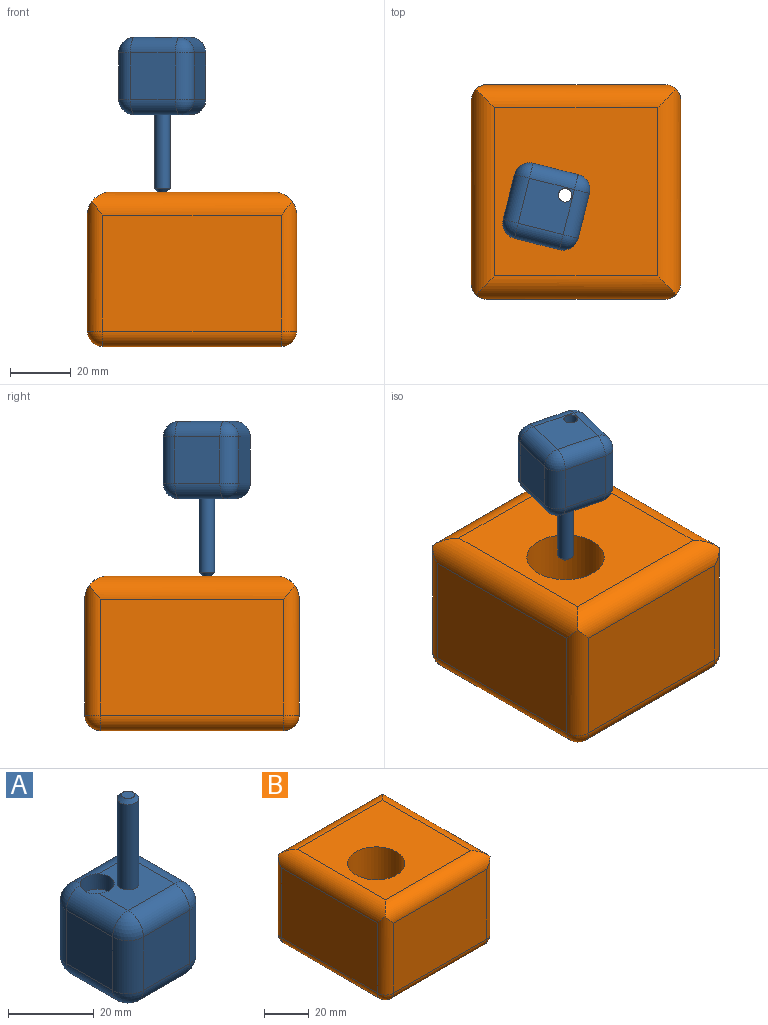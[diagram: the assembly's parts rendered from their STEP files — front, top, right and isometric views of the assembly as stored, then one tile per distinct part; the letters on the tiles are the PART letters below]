
ASSEMBLY  parts=2 mates=1
PART A: 32 faces, bbox 25.4x25.4x50.8 mm
  f0: plane 15.24x15.24mm, normal (0,0,1), area 174.5mm2, adj f2,f3,f19,f20,f28,f29
  f1: sphere r=5.08mm, area 40.3mm2, adj f2,f3,f9,f28
  f2: cylinder r=5.08mm len=15.24mm, axis (0,1,0), area 115.6mm2, adj f0,f1,f7,f15,f28
  f3: cylinder r=5.08mm len=15.24mm, axis (1,0,0), area 115.6mm2, adj f0,f1,f6,f16,f28
  f4: plane 15.24x15.24mm, normal (0,-1,0), area 232.3mm2, adj f14,f19,f22,f25
  f5: plane 15.24x15.24mm, normal (1,0,0), area 232.3mm2, adj f11,f20,f21,f25
  f6: plane 15.24x15.24mm, normal (0,1,0), area 232.3mm2, adj f3,f9,f11,f12
  f7: plane 15.24x15.24mm, normal (-1,0,0), area 232.3mm2, adj f2,f9,f13,f14
  f8: plane 15.24x15.24mm, normal (0,0,-1), area 216.4mm2, adj f12,f13,f21,f22,f26
  f9: cylinder r=5.08mm len=15.24mm, axis (0,0,1), area 121.6mm2, adj f1,f6,f7,f10
  f10: sphere r=5.08mm, area 40.5mm2, adj f9,f12,f13
  f11: cylinder r=5.08mm len=15.24mm, axis (0,0,-1), area 121.6mm2, adj f5,f6,f16,f17
  f12: cylinder r=5.08mm len=15.24mm, axis (-1,0,0), area 121.6mm2, adj f6,f8,f10,f17
  f13: cylinder r=5.08mm len=15.24mm, axis (0,-1,0), area 121.6mm2, adj f7,f8,f10,f18
  f14: cylinder r=5.08mm len=15.24mm, axis (0,0,-1), area 121.6mm2, adj f4,f7,f15,f18
  f15: sphere r=5.08mm, area 40.5mm2, adj f2,f14,f19
  f16: sphere r=5.08mm, area 40.5mm2, adj f3,f11,f20
  f17: sphere r=5.08mm, area 40.5mm2, adj f11,f12,f21
  f18: sphere r=5.08mm, area 40.5mm2, adj f13,f14,f22
  f19: cylinder r=5.08mm len=15.24mm, axis (-1,0,0), area 121.6mm2, adj f0,f4,f15,f23
  f20: cylinder r=5.08mm len=15.24mm, axis (0,-1,0), area 121.6mm2, adj f0,f5,f16,f23
  f21: cylinder r=5.08mm len=15.24mm, axis (0,1,0), area 121.6mm2, adj f5,f8,f17,f24
  f22: cylinder r=5.08mm len=15.24mm, axis (1,0,0), area 121.6mm2, adj f4,f8,f18,f24
  f23: sphere r=5.08mm, area 40.5mm2, adj f19,f20,f25
  f24: sphere r=5.08mm, area 40.5mm2, adj f21,f22,f25
  f25: cylinder r=5.08mm len=15.24mm, axis (0,0,1), area 121.6mm2, adj f4,f5,f23,f24
  f26: cylinder r=2.25mm len=21.03mm, axis (0,0,1), area 297mm2, adj f8,f27
  f27: plane 7.94x7.94mm, normal (0,0,1), area 33.6mm2, adj f26,f28
  f28: cylinder r=3.97mm len=7.94mm, axis (0,0,1), area 107.5mm2, adj f0,f1,f2,f3,f27
  f29: cylinder r=2.54mm len=24.4mm, axis (0,0,-1), area 389.4mm2, adj f0,f31
  f30: plane 3.08x3.08mm, normal (0,0,1), area 7.5mm2, adj f31
  f31: cone r=1.54mm half-angle=45deg, axis (0,0,-1), area 18.1mm2, adj f29,f30
PART B: 23 faces, bbox 68.8x70.5x50.8 mm
  f0: plane 58.65x38.1mm, normal (0,1,0), area 2234.6mm2, adj f6,f12,f18,f21
  f1: plane 60.33x38.1mm, normal (-1,0,0), area 2298.5mm2, adj f7,f10,f12,f13
  f2: plane 58.65x38.1mm, normal (0,-1,0), area 2234.6mm2, adj f9,f10,f14,f15
  f3: plane 60.33x38.1mm, normal (1,0,0), area 2298.5mm2, adj f8,f15,f19,f21
  f4: plane 55.25x53.57mm, normal (0,0,1), area 2453mm2, adj f6,f7,f8,f9,f22
  f5: plane 60.33x58.65mm, normal (0,0,-1), area 3031.6mm2, adj f13,f14,f18,f19,f22
  f6: cylinder r=7.62mm len=65.84mm, axis (1,0,0), area 731.3mm2, adj f0,f4,f7,f8,f12,f21
  f7: cylinder r=7.62mm len=67.51mm, axis (0,1,0), area 751.3mm2, adj f1,f4,f6,f9,f10,f12
  f8: cylinder r=7.62mm len=67.51mm, axis (0,-1,0), area 751.3mm2, adj f3,f4,f6,f9,f15,f21
  f9: cylinder r=7.62mm len=65.84mm, axis (-1,0,0), area 731.3mm2, adj f2,f4,f7,f8,f10,f15
  f10: cylinder r=5.08mm len=42.62mm, axis (0,0,-1), area 322.8mm2, adj f1,f2,f7,f9,f11
  f11: sphere r=5.08mm, area 40.5mm2, adj f10,f13,f14
  f12: cylinder r=5.08mm len=42.62mm, axis (0,0,1), area 322.8mm2, adj f0,f1,f6,f7,f16
  f13: cylinder r=5.08mm len=60.33mm, axis (0,-1,0), area 481.4mm2, adj f1,f5,f11,f16
  f14: cylinder r=5.08mm len=58.65mm, axis (1,0,0), area 468mm2, adj f2,f5,f11,f17
  f15: cylinder r=5.08mm len=42.62mm, axis (0,0,1), area 322.8mm2, adj f2,f3,f8,f9,f17
  f16: sphere r=5.08mm, area 40.5mm2, adj f12,f13,f18
  f17: sphere r=5.08mm, area 40.5mm2, adj f14,f15,f19
  f18: cylinder r=5.08mm len=58.65mm, axis (-1,0,0), area 468mm2, adj f0,f5,f16,f20
  f19: cylinder r=5.08mm len=60.33mm, axis (0,1,0), area 481.4mm2, adj f3,f5,f17,f20
  f20: sphere r=5.08mm, area 40.5mm2, adj f18,f19,f21
  f21: cylinder r=5.08mm len=42.62mm, axis (0,0,-1), area 322.8mm2, adj f0,f3,f6,f8,f20
  f22: cylinder r=12.7mm len=50.8mm, axis (0,0,1), area 4053.7mm2, adj f4,f5
PLACE A rot(axis=(-0.12,-0.99,0),180deg) t=(-36.92,-6.83,96.78)mm
PLACE B t=(1.6,16.9,-4.82)mm fixed
MATE revolute B.f22 <-> A.f29  axis (0,0,1) through (-36.92,-6.83,45.98)mm
